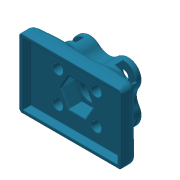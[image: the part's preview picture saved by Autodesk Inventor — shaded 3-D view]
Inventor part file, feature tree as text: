
AUTODESK INVENTOR PART (.ipt)
format: ipt  version: 2014 (Build 180170000, 170)  size: 941,568 bytes
history: native  units: mm
features: fillet x12, sketch x8, extrude x6, plane x1, loft x1, other x1
ambient origin geometry x8: Origin, YZ Plane, XZ Plane, XY Plane, X Axis, Y Axis, Z Axis, Center Point
bodies: Solid1 (feature_tree)
feature tree (29):
  extrude  "Extrusion1"  Depth=13.0mm
  extrude  "Extrusion2"  Depth=12.0mm
  sketch  "Sketch3"  dims[d5=25.0mm d7=13.0mm d8=0.0mm]
  sketch  "Sketch5"  dims[d11=9.0mm d12=10.5mm]
  plane  "Work Plane2"
  loft  "Loft1"
  extrude  "Extrusion3"  Depth=9.0mm
  extrude  "Extrusion4"  Depth=10.5mm
  extrude  "Extrusion5"  TaperAngle=45.0deg  [1 undecoded]
  fillet  "Fillet1"  Radius=10.0mm
  fillet  "Fillet2"  Radius=5.25mm
  fillet  "Fillet3"  Radius=18.0mm
  fillet  "Fillet4"  Radius=4.0mm
  fillet  "Fillet5"  Radius=46.0mm
  fillet  "Fillet6"  Radius=68.0mm
  fillet  "Fillet7"  [1 undecoded]
  fillet  "Fillet8"  Radius=5.25mm
  fillet  "Fillet9"  Radius=4.4mm
  fillet  "Fillet10"  Radius=3.5mm
  fillet  "Fillet11"  Radius=3.9mm
  extrude  "Extrusion6"  Depth=0.5mm
  fillet  "Fillet12"  Radius=4.0mm
  sketch  "Sketch1"  dims[d0=6.35mm d1=13.0mm]
  sketch  "Sketch2"  dims[d2=20.0mm d4=12.0mm]
  sketch  "Sketch4"  dims[d9=9.0mm d10=9.0mm]
  other  "Edges1"
  sketch  "Sketch6"  dims[d13=45.0deg d14=45.0deg d15=10.0mm d16=5.25mm d17=0.0mm d18=18.0mm d19=4.0mm d20=46.0mm d21=68.0mm]
  sketch  "Sketch7"  dims[d22=0.0mm d23=90.0deg d24=0.0mm d25=90.0deg d26=0.0mm d27=90.0deg d28=5.25mm d29=0.0mm d30=4.4mm d31=0.0mm d32=3.5mm d33=3.9mm]
  sketch  "Sketch8"  dims[d34=4.4mm d35=-1.396263mm d36=4.0mm d37=4.0mm d38=4.0mm d39=4.0mm d40=0.75mm d41=1.5mm d42=1.0mm d43=0.5mm d44=0.5mm d45=0.5mm d46=0.5mm d47=4.4mm d48=0.0mm d49=0.5mm]
note: 2 required parameter values undecoded (feature->parameter linkage not recoverable at this tier; creation-order binding heuristic only, values carry confidence <= 0.55)
